# Revit family: WIL2_63_UN_Downlighter_ETK
name_source: partatom
category: Lighting Fixtures
revit_build: Autodesk Revit 2017 (Build: 20190508_0315(x64)
units: mm (PartAtom-declared; Revit-internal decimal feet)

## family parameters
Always vertical = Yes
Cut with Voids When Loaded = No
Light Source = No
OmniClass Number = 23.80.70.11.14.11
OmniClass Title = Downlights
Part Type = Normal
Room Calculation Point = Yes
Round Connector Dimension = Use Diameter
Shared = No
Work Plane-Based = No

## types (8) — shared parameters
Assembly Code = 63.0
Bundle = 70°
Description = Downlighter
IfcExportAs = IfcLightFixtureType
IfcExportType = USERDEFINED
Lamp = LED
Luminaire_Body_Material = PPS Plastic
Manufacturer = ETK licht B.V.
Model = WILL.2
URL = https://www.etk.nl
Voltage = 230 V

## per-type parameters (varying)
| type | Apparent Load | Light Source | Wattage Comments |
| WIL.2100.10 - 13W / 1980lm / 3000K | 13 VA | WIL.2 - Lightsource : WIL.2100.10 - LED 13W / 1980lm / 3000K | 13W |
| WIL.2200.10 - 13W / 2020lm / 4000K | 13 VA | WIL.2 - Lightsource : WIL.2200.10 - LED 13W / 2020lm / 4000K | 13W |
| WIL.2300.10 - 18W / 2425lm / 3000K | 18 VA | WIL.2 - Lightsource : WIL.2300.10 - LED 18W / 2425lm / 3000K | 18W |
| WIL.2400.10 - 18W / 2500lm / 4000K | 18 VA | WIL.2 - Lightsource : WIL.2400.10 - LED 18W / 2500lm / 4000K | 18W |
| WIL.2103.10 - 13W / 1980lm / 3000K | 13 VA | WIL.2 - Lightsource : WIL.2103.10 - LED 13W / 1980lm / 3000K | 13W |
| WIL.2203.10 - 13W / 2020lm / 4000K | 13 VA | WIL.2 - Lightsource : WIL.2203.10 - LED 13W / 2020lm / 4000K | 13W |
| WIL.2303.10 - 18W / 2425lm / 3000K | 18 VA | WIL.2 - Lightsource : WIL.2303.10 - LED 18W / 2425lm / 3000K | 18W |
| WIL.2403.10 - 18W / 2500lm / 4000K | 18 VA | WIL.2 - Lightsource : WIL.2403.10 - LED 18W / 2500lm / 4000K | 18W |

## geometry (parser evidence)
native form markers: Sweep x6
no freeform markers — native parametric forms only
